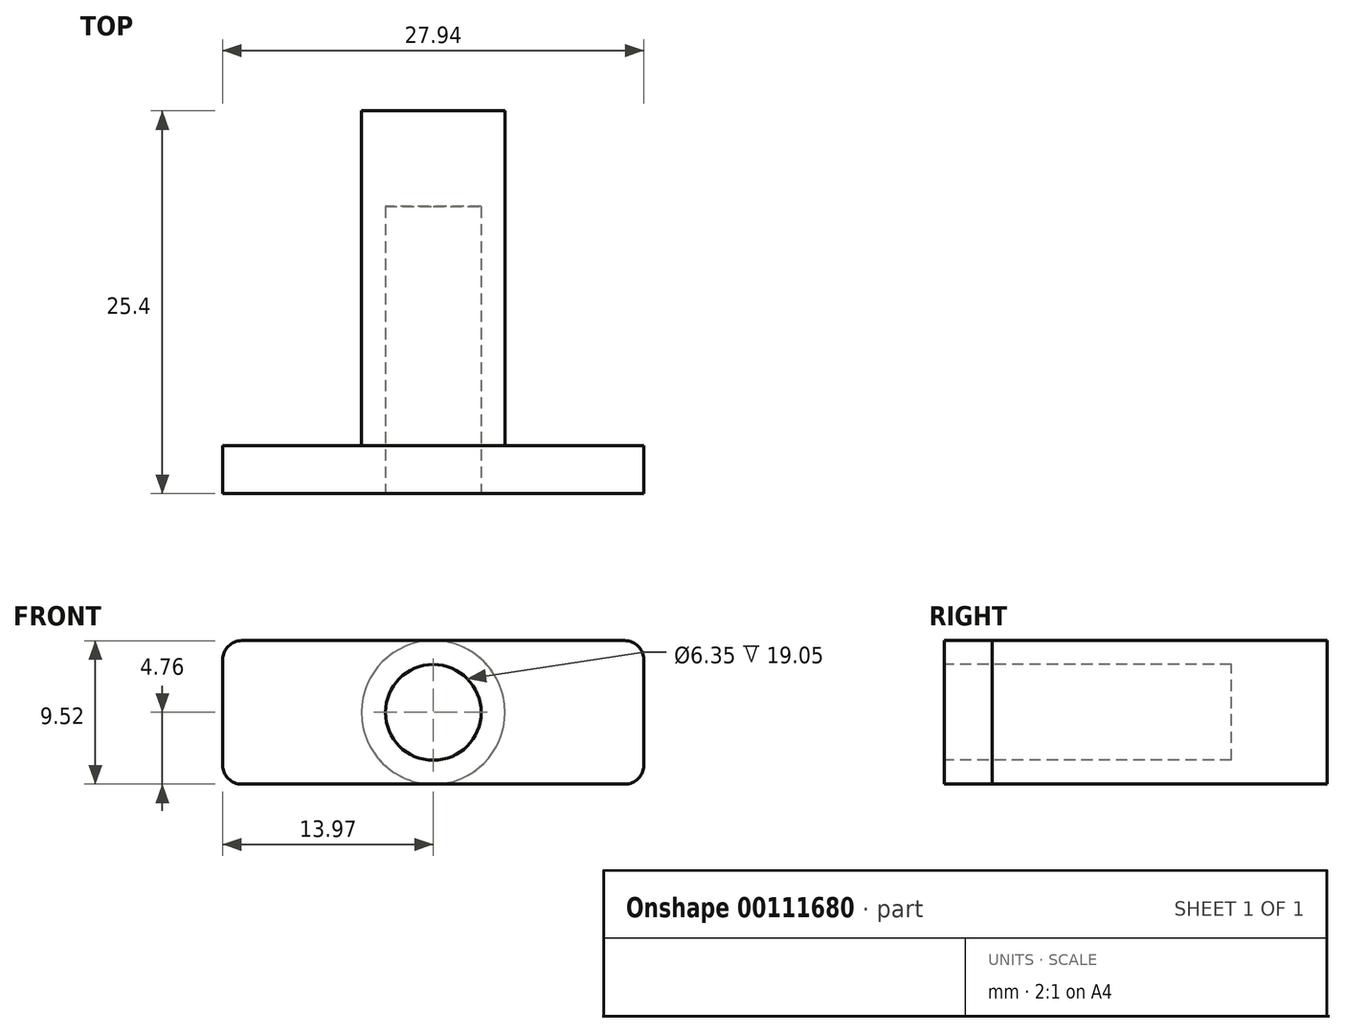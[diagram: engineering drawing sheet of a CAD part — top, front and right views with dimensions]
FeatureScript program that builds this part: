
annotation { "Feature Type Name" : "Feature", "Feature Type Description" : "" }
export const myFeature = defineFeature(function(context is Context, id is Id, definition is map)
    precondition{}
    {
        {
            var Q0;
            Q0=qCreatedBy(makeId("Front.planeOp"),FACE);
            var sketch = newSketch(context, id + "F0", { "sketchPlane" : qUnion([Q0])});
            skCircle(sketch, "E0", {"center": v(0, 0) * mm, "radius": 4.76 * mm});
            skSolve(sketch);
        }
        {
            var Q0;
            Q0=makeQuery(id+"F0.imprint","IMPRINT",FACE,{"disambiguationData":[TD([[makeQuery(id+"F0.imprint","IMPRINT",EDGE,{"derivedFrom":sQuery(id+"F0.wireOp",EDGE,"E0")}),1.0]])]});
            extrude(context, id + "F1", {"entities" : qUnion([Q0]), "depth" : 25.4 * mm});
        }
        {
            var Q0;
            Q0=makeQuery(id+"F1.opExtrude","CAP_FACE",FACE,{"disambiguationData":[OSD([sQuery(id+"F0.wireOp",EDGE,"E0")])],"isStart":false});
            var sketch = newSketch(context, id + "F2", { "sketchPlane" : qUnion([Q0])});
            skCircle(sketch, "E1", {"center": v(0, 0) * mm, "radius": 3.18 * mm});
            skSolve(sketch);
        }
        {
            var Q0;
            Q0=makeQuery(id+"F2.imprint","IMPRINT",FACE,{"disambiguationData":[TD([[makeQuery(id+"F2.imprint","IMPRINT",EDGE,{"derivedFrom":sQuery(id+"F2.wireOp",EDGE,"E1")}),1.0]])]});
            extrude(context, id + "F3", {"entities" : qUnion([Q0]), "operationType" : NewBodyOperationType.REMOVE, "oppositeDirection" : true, "depth" : 19.05 * mm});
        }
        {
            var Q0;
            Q0=makeQuery(id+"F1.opExtrude","CAP_FACE",FACE,{"disambiguationData":[OSD([sQuery(id+"F0.wireOp",EDGE,"E0")])],"isStart":false});
            var sketch = newSketch(context, id + "F4", { "sketchPlane" : qUnion([Q0])});
            skLineSegment(sketch, "E2", {"start": v(0, 4.76) * mm, "end": v(12.7, 4.76) * mm});
            skLineSegment(sketch, "E3", {"start": v(0, 4.76) * mm, "end": v(-12.7, 4.76) * mm});
            skLineSegment(sketch, "E4", {"start": v(0, -4.76) * mm, "end": v(-12.7, -4.76) * mm});
            skLineSegment(sketch, "E5", {"start": v(-13.97, -3.5) * mm, "end": v(-13.97, 3.5) * mm});
            skLineSegment(sketch, "E6", {"start": v(13.97, 3.5) * mm, "end": v(13.97, -3.5) * mm});
            skLineSegment(sketch, "E7", {"start": v(12.7, -4.76) * mm, "end": v(0, -4.76) * mm});
            skPoint(sketch, "E8.visualSharp", {"position": v(13.97, 4.76) * mm});
            skArc(sketch, "E8.filletArc", {"start": v(13.97, 3.5) * mm, "mid": v(13.6, 4.4) * mm, "end": v(12.7, 4.76) * mm});
            skPoint(sketch, "E9.visualSharp", {"position": v(13.97, -4.76) * mm});
            skArc(sketch, "E9.filletArc", {"start": v(12.7, -4.76) * mm, "mid": v(13.6, -4.4) * mm, "end": v(13.97, -3.5) * mm});
            skPoint(sketch, "E10.visualSharp", {"position": v(-13.97, -4.76) * mm});
            skArc(sketch, "E10.filletArc", {"start": v(-13.97, -3.5) * mm, "mid": v(-13.6, -4.4) * mm, "end": v(-12.7, -4.76) * mm});
            skPoint(sketch, "E11.visualSharp", {"position": v(-13.97, 4.76) * mm});
            skArc(sketch, "E11.filletArc", {"start": v(-12.7, 4.76) * mm, "mid": v(-13.6, 4.4) * mm, "end": v(-13.97, 3.5) * mm});
            skSolve(sketch);
        }
        {
            var Q0;
            {var subQ0=sQuery(id+"F4.wireOp",EDGE,"E3");Q0=makeQuery(id+"F4.imprint","IMPRINT",FACE,{"disambiguationData":[TD([[makeQuery(id+"F4.imprint","IMPRINT",EDGE,{"derivedFrom":subQ0}),1.0]])]});}
            var Q1;
            {var subQ0=sQuery(id+"F4.wireOp",EDGE,"E2");Q1=makeQuery(id+"F4.imprint","IMPRINT",FACE,{"disambiguationData":[TD([[makeQuery(id+"F4.imprint","IMPRINT",EDGE,{"derivedFrom":subQ0}),-1.0]])]});}
            extrude(context, id + "F5", {"entities" : qUnion([Q0, Q1]), "operationType" : NewBodyOperationType.ADD, "oppositeDirection" : true, "depth" : 3.17 * mm});
        }
    });
